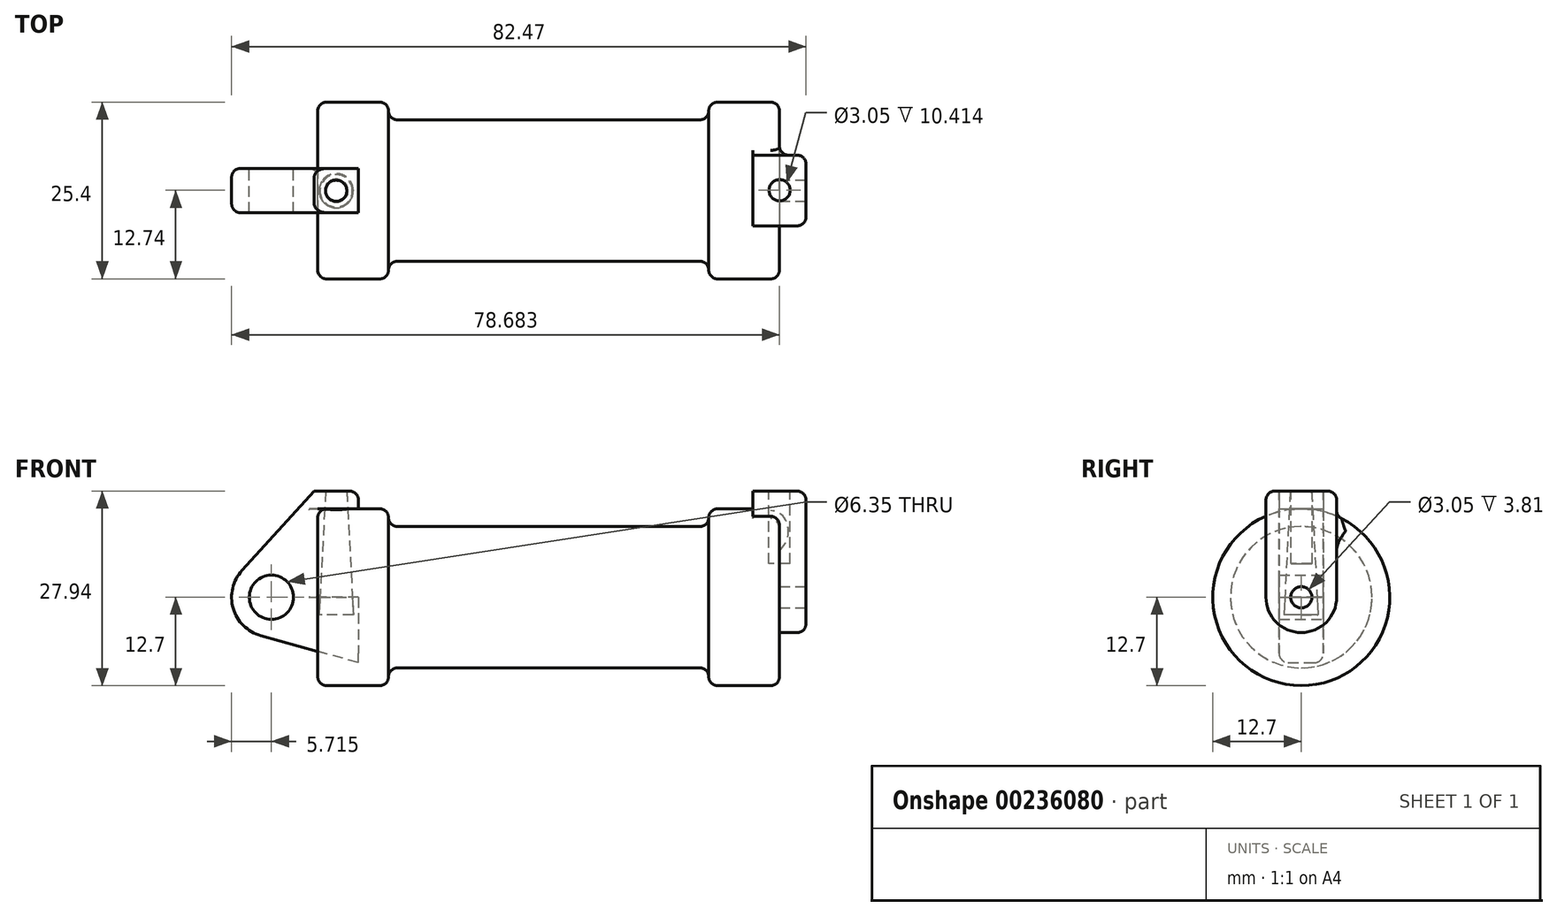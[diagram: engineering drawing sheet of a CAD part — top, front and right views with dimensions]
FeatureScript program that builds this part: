
annotation { "Feature Type Name" : "Feature", "Feature Type Description" : "" }
export const myFeature = defineFeature(function(context is Context, id is Id, definition is map)
    precondition{}
    {
        {
            var Q0;
            Q0=qCreatedBy(makeId("Front.planeOp"),FACE);
            var sketch = newSketch(context, id + "F0", { "sketchPlane" : qUnion([Q0])});
            skLineSegment(sketch, "E0", {"start": v(0, 0) * mm, "end": v(0, 12.7) * mm});
            skLineSegment(sketch, "E1", {"start": v(0, 12.7) * mm, "end": v(10.16, 12.7) * mm});
            skLineSegment(sketch, "E2", {"start": v(10.16, 12.7) * mm, "end": v(10.16, 10.16) * mm});
            skLineSegment(sketch, "E3", {"start": v(10.16, 10.16) * mm, "end": v(56.13, 10.16) * mm});
            skLineSegment(sketch, "E4", {"start": v(56.13, 10.16) * mm, "end": v(56.13, 12.7) * mm});
            skLineSegment(sketch, "E5", {"start": v(56.13, 12.7) * mm, "end": v(66.3, 12.7) * mm});
            skLineSegment(sketch, "E6", {"start": v(66.3, 12.7) * mm, "end": v(66.3, 0) * mm});
            skLineSegment(sketch, "E7", {"start": v(66.3, 0) * mm, "end": v(0, 0) * mm});
            skLineSegment(sketch, "E8", {"start": v(5.84, 15.24) * mm, "end": v(-0.5, 15.24) * mm});
            skLineSegment(sketch, "E9", {"start": v(-0.5, 15.24) * mm, "end": v(-10.88, 3.85) * mm});
            skLineSegment(sketch, "E10", {"start": v(0, 0) * mm, "end": v(-6.65, 0) * mm});
            skCircle(sketch, "E11", {"center": v(-6.65, 0) * mm, "radius": 5.72 * mm});
            skCircle(sketch, "E12", {"center": v(-6.65, 0) * mm, "radius": 3.18 * mm});
            skLineSegment(sketch, "E13", {"start": v(5.84, 15.24) * mm, "end": v(5.84, -9.4) * mm});
            skLineSegment(sketch, "E14", {"start": v(5.84, -9.4) * mm, "end": v(-8.18, -5.5) * mm});
            skSolve(sketch);
        }
        {
            var Q0;
            {var subQ0=sQuery(id+"F0.wireOp",EDGE,"E2");Q0=makeQuery(id+"F0.imprint","IMPRINT",FACE,{"disambiguationData":[TD([[makeQuery(id+"F0.imprint","IMPRINT",EDGE,{"derivedFrom":subQ0}),-1.0]])]});}
            var Q1;
            {var subQ0=sQuery(id+"F0.wireOp",EDGE,"E0");Q1=makeQuery(id+"F0.imprint","IMPRINT",FACE,{"disambiguationData":[TD([[makeQuery(id+"F0.imprint","IMPRINT",EDGE,{"derivedFrom":subQ0}),-1.0]])]});}
            var Q2;
            Q2=sQuery(id+"F0.wireOp",EDGE,"E1");
            var Q3;
            Q3=sQuery(id+"F0.wireOp",EDGE,"E3");
            var Q4;
            Q4=sQuery(id+"F0.wireOp",EDGE,"E7");
            revolve(context, id + "F1", {"entities" : qUnion([Q0, Q1]), "surfaceEntities" : qUnion([Q2, Q3]), "axis" : qUnion([Q4]), "revolveType" : RevolveType.FULL});
        }
        {
            var Q0;
            {var subQ3=sQuery(id+"F0.wireOp",EDGE,"E0");Q0=makeQuery(id+"F0.imprint","IMPRINT",FACE,{"disambiguationData":[TD([[makeQuery(id+"F0.imprint","IMPRINT",EDGE,{"derivedFrom":subQ3}),1.0]])]});}
            var Q1;
            {var subQ4=sQuery(id+"F0.wireOp",EDGE,"E12");Q1=makeQuery(id+"F0.imprint","IMPRINT",FACE,{"disambiguationData":[TD([[makeQuery(id+"F0.imprint","IMPRINT",EDGE,{"derivedFrom":subQ4}),-1.0]])]});}
            var Q2;
            {var subQ0=sQuery(id+"F0.wireOp",EDGE,"E14");Q2=makeQuery(id+"F0.imprint","IMPRINT",FACE,{"disambiguationData":[TD([[makeQuery(id+"F0.imprint","IMPRINT",EDGE,{"derivedFrom":subQ0}),-1.0]])]});}
            extrude(context, id + "F2", {"entities" : qUnion([Q0, Q1, Q2]), "endBound" : BoundingType.SYMMETRIC, "depth" : 6.35 * mm});
        }
        {
            var Q0;
            Q0=makeQuery(id+"F1.opRevolve","SWEPT_FACE",FACE,{"disambiguationData":[OSD([sQuery(id+"F0.wireOp",EDGE,"E6")])]});
            var sketch = newSketch(context, id + "F3", { "sketchPlane" : qUnion([Q0])});
            skCircle(sketch, "E15", {"center": v(0, 0) * mm, "radius": 5.08 * mm});
            skCircle(sketch, "E16", {"center": v(0, 0) * mm, "radius": 1.52 * mm});
            skLineSegment(sketch, "E17", {"start": v(-5.08, 0) * mm, "end": v(-5.08, 15.24) * mm});
            skLineSegment(sketch, "E18", {"start": v(-5.08, 15.24) * mm, "end": v(0, 15.24) * mm});
            skLineSegment(sketch, "E19.MirrorCS", {"start": v(5.08, 0) * mm, "end": v(5.08, 15.24) * mm});
            skLineSegment(sketch, "E20.MirrorCS", {"start": v(5.08, 15.24) * mm, "end": v(0, 15.24) * mm});
            skSolve(sketch);
        }
        {
            var Q0;
            Q0 = qSketchRegion(id + "F3", true);
            extrude(context, id + "F4", {"entities" : qUnion([Q0]), "operationType" : NewBodyOperationType.ADD, "endBound" : BoundingType.SYMMETRIC, "oppositeDirection" : true, "depth" : 7.62 * mm});
        }
        {
            var Q0;
            Q0=makeQuery(id+"F2.opExtrude","SWEPT_FACE",FACE,{"disambiguationData":[OSD([sQuery(id+"F0.wireOp",EDGE,"E8")])]});
            var sketch = newSketch(context, id + "F5", { "sketchPlane" : qUnion([Q0])});
            skCircle(sketch, "E21", {"center": v(2.65, -0.04) * mm, "radius": 1.52 * mm});
            skSolve(sketch);
        }
        {
            var Q0;
            Q0=makeQuery(id+"F5.imprint","IMPRINT",FACE,{"disambiguationData":[TD([[makeQuery(id+"F5.imprint","IMPRINT",EDGE,{"derivedFrom":sQuery(id+"F5.wireOp",EDGE,"E21")}),1.0]])]});
            extrude(context, id + "F6", {"entities" : qUnion([Q0]), "operationType" : NewBodyOperationType.REMOVE, "oppositeDirection" : true, "depth" : 17.78 * mm, "hasDraft" : true, "draftAngle" : 3 * degree});
        }
        {
            var Q0;
            Q0=makeQuery(id+"F4.opExtrude","SWEPT_FACE",FACE,{"disambiguationData":[OSD([sQuery(id+"F3.wireOp",EDGE,"E18"),sQuery(id+"F3.wireOp",EDGE,"E20.MirrorCS")])]});
            var sketch = newSketch(context, id + "F7", { "sketchPlane" : qUnion([Q0])});
            skCircle(sketch, "E22", {"center": v(66.31, 0.04) * mm, "radius": 1.52 * mm});
            skSolve(sketch);
        }
        {
            var Q0;
            Q0=makeQuery(id+"F7.imprint","IMPRINT",FACE,{"disambiguationData":[TD([[makeQuery(id+"F7.imprint","IMPRINT",EDGE,{"derivedFrom":sQuery(id+"F7.wireOp",EDGE,"E22")}),1.0]])]});
            extrude(context, id + "F8", {"entities" : qUnion([Q0]), "operationType" : NewBodyOperationType.REMOVE, "oppositeDirection" : true, "depth" : 10.4 * mm});
        }
        {
            var Q0;
            Q0=makeQuery(id+"F1.opRevolve","SWEPT_EDGE",EDGE,{"disambiguationData":[OSD([sQuery(id+"F0.wireOp",EDGE,"E1"),sQuery(id+"F0.wireOp",EDGE,"E2")])]});
            var Q1;
            Q1=makeQuery(id+"F1.opRevolve","SWEPT_EDGE",EDGE,{"disambiguationData":[OSD([sQuery(id+"F0.wireOp",EDGE,"E5"),sQuery(id+"F0.wireOp",EDGE,"E6")])]});
            var Q2;
            Q2=makeQuery(id+"F1.opRevolve","SWEPT_EDGE",EDGE,{"disambiguationData":[OSD([sQuery(id+"F0.wireOp",EDGE,"E4"),sQuery(id+"F0.wireOp",EDGE,"E5")])]});
            var Q3;
            Q3=makeQuery(id+"F1.opRevolve","SWEPT_EDGE",EDGE,{"disambiguationData":[OSD([sQuery(id+"F0.wireOp",EDGE,"E2"),sQuery(id+"F0.wireOp",EDGE,"E3")])]});
            var Q4;
            Q4=makeQuery(id+"F1.opRevolve","SWEPT_EDGE",EDGE,{"disambiguationData":[OSD([sQuery(id+"F0.wireOp",EDGE,"E3"),sQuery(id+"F0.wireOp",EDGE,"E4")])]});
            var Q5;
            Q5=makeQuery(id+"F1.opRevolve","SWEPT_EDGE",EDGE,{"disambiguationData":[OSD([sQuery(id+"F0.wireOp",EDGE,"E0"),sQuery(id+"F0.wireOp",EDGE,"E1")])]});
            var Q6;
            Q6=makeQuery(id+"F2.opExtrude","SWEPT_EDGE",EDGE,{"disambiguationData":[OSD([sQuery(id+"F0.wireOp",EDGE,"E8"),sQuery(id+"F0.wireOp",EDGE,"E13")])]});
            var Q7;
            Q7=makeQuery(id+"F4.opExtrude","SWEPT_EDGE",EDGE,{"disambiguationData":[OSD([sQuery(id+"F3.wireOp",EDGE,"E17"),sQuery(id+"F3.wireOp",EDGE,"E18")])]});
            var Q8;
            Q8=makeQuery(id+"F4.opExtrude","SWEPT_EDGE",EDGE,{"disambiguationData":[OSD([sQuery(id+"F3.wireOp",EDGE,"E19.MirrorCS"),sQuery(id+"F3.wireOp",EDGE,"E20.MirrorCS")])]});
            var Q9;
            Q9=makeQuery(id+"F4.opExtrude","CAP_EDGE",EDGE,{"disambiguationData":[OSD([sQuery(id+"F3.wireOp",EDGE,"E17")])],"isStart":true});
            var Q10;
            Q10=makeQuery(id+"F4.opExtrude","CAP_EDGE",EDGE,{"disambiguationData":[OSD([sQuery(id+"F3.wireOp",EDGE,"E18"),sQuery(id+"F3.wireOp",EDGE,"E20.MirrorCS")])],"isStart":true});
            var Q11;
            Q11=makeQuery(id+"F2.opExtrude","CAP_EDGE",EDGE,{"disambiguationData":[OSD([sQuery(id+"F0.wireOp",EDGE,"E9")])],"isStart":false});
            var Q12;
            Q12=makeQuery(id+"F2.opExtrude","CAP_EDGE",EDGE,{"disambiguationData":[OSD([sQuery(id+"F0.wireOp",EDGE,"E9")])],"isStart":true});
            var Q13;
            Q13=makeQuery(id+"F4.boolean.opBoolean","INTERSECT",EDGE,{"derivedFrom":[makeQuery(id+"F1.opRevolve","SWEPT_FACE",FACE,{"disambiguationData":[OSD([sQuery(id+"F0.wireOp",EDGE,"E5")])]}),makeQuery(id+"F4.opExtrude","SWEPT_FACE",FACE,{"disambiguationData":[OSD([sQuery(id+"F3.wireOp",EDGE,"E19.MirrorCS")])]})]});
            var Q14;
            Q14=makeQuery(id+"F2.opExtrude","CAP_EDGE",EDGE,{"disambiguationData":[OSD([sQuery(id+"F0.wireOp",EDGE,"E0")])],"isStart":true});
            fillet(context, id + "F9", {"entities" : qUnion([Q0, Q1, Q2, Q3, Q4, Q5, Q6, Q7, Q8, Q9, Q10, Q11, Q12, Q13, Q14]), "radius" : 1.27 * mm, "tangentPropagation" : true, "allowEdgeOverflow" : false});
        }
    });
